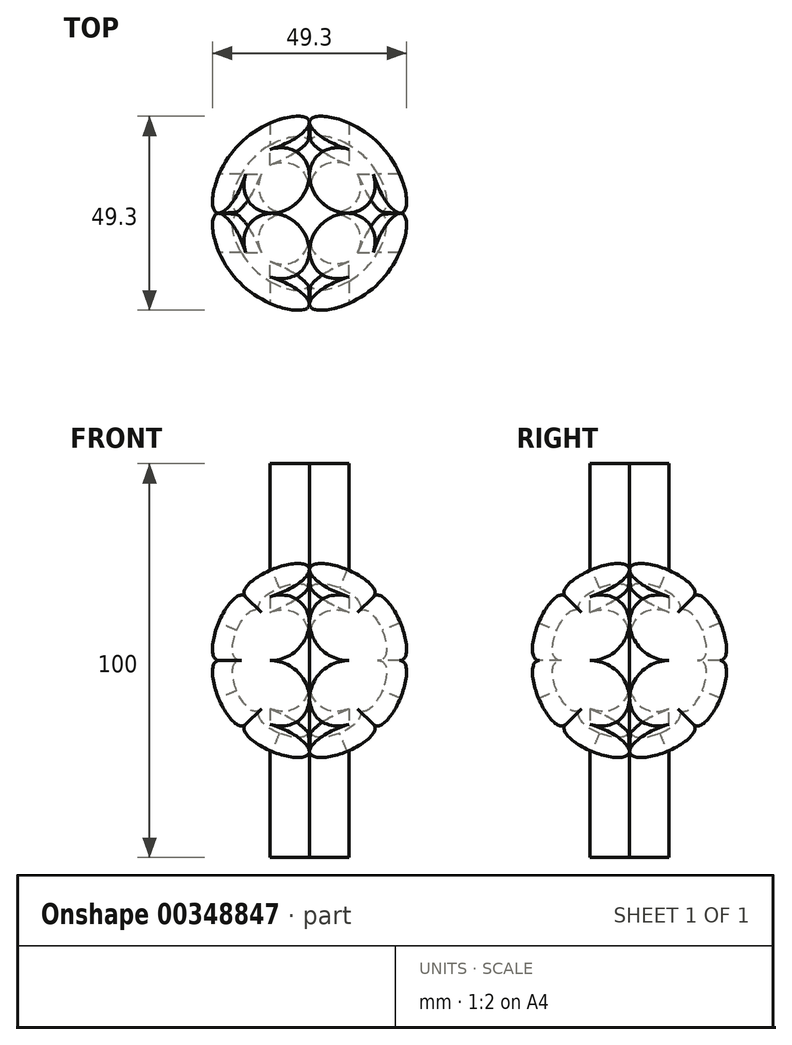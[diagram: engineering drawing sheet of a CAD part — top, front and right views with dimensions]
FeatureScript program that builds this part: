
annotation { "Feature Type Name" : "Feature", "Feature Type Description" : "" }
export const myFeature = defineFeature(function(context is Context, id is Id, definition is map)
    precondition{}
    {
        {
            var Q0;
            Q0=qCreatedBy(makeId("Front.planeOp"),FACE);
            var sketch = newSketch(context, id + "F0", { "sketchPlane" : qUnion([Q0])});
            skArc(sketch, "E0", {"start": v(0, -25) * mm, "mid": v(25, 0) * mm, "end": v(0, 25) * mm});
            skLineSegment(sketch, "E1", {"start": v(0, 25) * mm, "end": v(0, 20) * mm});
            skArc(sketch, "E2.0", {"start": v(0, -20) * mm, "mid": v(20, 0) * mm, "end": v(0, 20) * mm});
            skLineSegment(sketch, "E3.trimOffspring", {"start": v(0, -20) * mm, "end": v(0, -25) * mm});
            skSolve(sketch);
        }
        {
            var Q0;
            {var subQ0=sQuery(id+"F0.wireOp",EDGE,"E0");Q0=makeQuery(id+"F0.imprint","IMPRINT",FACE,{"disambiguationData":[TD([[makeQuery(id+"F0.imprint","IMPRINT",EDGE,{"derivedFrom":subQ0}),1.0]])]});}
            var Q1;
            Q1=sQuery(id+"F0.wireOp",EDGE,"E1");
            revolve(context, id + "F1", {"entities" : qUnion([Q0]), "axis" : qUnion([Q1]), "revolveType" : RevolveType.FULL});
        }
        {
            var Q0;
            Q0=qCreatedBy(makeId("Front.planeOp"),FACE);
            var sketch = newSketch(context, id + "F2", { "sketchPlane" : qUnion([Q0])});
            skArc(sketch, "E4", {"start": v(0, 10) * mm, "mid": v(2.93, 2.93) * mm, "end": v(10, 0) * mm});
            skArc(sketch, "E5.1.0", {"start": v(-10, 0) * mm, "mid": v(-2.93, 2.93) * mm, "end": v(0, 10) * mm});
            skArc(sketch, "E5.2.0", {"start": v(0, -10) * mm, "mid": v(-2.93, -2.93) * mm, "end": v(-10, 0) * mm});
            skArc(sketch, "E5.3.0", {"start": v(10, 0) * mm, "mid": v(2.93, -2.93) * mm, "end": v(0, -10) * mm});
            skPoint(sketch, "E5.center", {"position": v(0, 0) * mm});
            skSolve(sketch);
        }
        {
            var Q0;
            Q0=makeQuery(id+"F2.imprint","IMPRINT",FACE,{"disambiguationData":[TD([[makeQuery(id+"F2.imprint","IMPRINT",EDGE,{"derivedFrom":sQuery(id+"F2.wireOp",EDGE,"E4")}),-1.0]])]});
            extrude(context, id + "F3", {"entities" : qUnion([Q0]), "endBound" : BoundingType.SYMMETRIC, "oppositeDirection" : true, "depth" : 100 * mm, "hasSecondDirection" : true, "secondDirectionBound" : SecondDirectionBoundingType.THROUGH_ALL, "secondDirectionOppositeDirection" : false, "secondDirectionDepth" : 25 * mm});
        }
        {
            var Q0;
            Q0=qCreatedBy(makeId("Top.planeOp"),FACE);
            var sketch = newSketch(context, id + "F4", { "sketchPlane" : qUnion([Q0])});
            skLineSegment(sketch, "E6", {"start": v(-40.96, 0) * mm, "end": v(40.96, 0) * mm, "construction": true});
            skLineSegment(sketch, "E7", {"start": v(0, 49.6) * mm, "end": v(0, -63.23) * mm, "construction": true});
            skSolve(sketch);
        }
        {
            var Q0;
            Q0=makeQuery(id+"F3.opExtrude","SWEPT_BODY",BODY,{"disambiguationData":[OSD([sQuery(id+"F2.wireOp",EDGE,"E4"),sQuery(id+"F2.wireOp",EDGE,"E5.1.0"),sQuery(id+"F2.wireOp",EDGE,"E5.2.0"),sQuery(id+"F2.wireOp",EDGE,"E5.3.0")])]});
            var Q1;
            Q1=sQuery(id+"F4.wireOp",EDGE,"E6");
            circularPattern(context, id + "F5", {"entities" : qUnion([Q0]), "axis" : qUnion([Q1]), "angle" : 360 * degree, "instanceCount" : 8, "equalSpace" : true});
        }
        {
            var Q0;
            Q0=qCreatedBy(makeId("Right.planeOp"),FACE);
            var sketch = newSketch(context, id + "F6", { "sketchPlane" : qUnion([Q0])});
            skLineSegment(sketch, "E8", {"start": v(-65.3, 0) * mm, "end": v(60.96, 0) * mm, "construction": true});
            skLineSegment(sketch, "E9", {"start": v(0, 65.88) * mm, "end": v(0, -65.12) * mm, "construction": true});
            skSolve(sketch);
        }
        {
            var Q0;
            Q0=makeQuery(id+"F5.opPattern","COPY",BODY,{"derivedFrom":makeQuery(id+"F3.opExtrude","SWEPT_BODY",BODY,{"disambiguationData":[OSD([sQuery(id+"F2.wireOp",EDGE,"E4"),sQuery(id+"F2.wireOp",EDGE,"E5.1.0"),sQuery(id+"F2.wireOp",EDGE,"E5.2.0"),sQuery(id+"F2.wireOp",EDGE,"E5.3.0")])]}),"instanceName":"2"});
            var Q1;
            Q1=sQuery(id+"F6.wireOp",EDGE,"E8");
            circularPattern(context, id + "F7", {"entities" : qUnion([Q0]), "axis" : qUnion([Q1]), "angle" : 360 * degree, "instanceCount" : 8, "equalSpace" : true});
        }
        {
            var Q0;
            Q0=makeQuery(id+"F3.opExtrude","SWEPT_BODY",BODY,{"disambiguationData":[OSD([sQuery(id+"F2.wireOp",EDGE,"E4"),sQuery(id+"F2.wireOp",EDGE,"E5.1.0"),sQuery(id+"F2.wireOp",EDGE,"E5.2.0"),sQuery(id+"F2.wireOp",EDGE,"E5.3.0")])]});
            var Q1;
            Q1=makeQuery(id+"F5.opPattern","COPY",BODY,{"derivedFrom":makeQuery(id+"F3.opExtrude","SWEPT_BODY",BODY,{"disambiguationData":[OSD([sQuery(id+"F2.wireOp",EDGE,"E4"),sQuery(id+"F2.wireOp",EDGE,"E5.1.0"),sQuery(id+"F2.wireOp",EDGE,"E5.2.0"),sQuery(id+"F2.wireOp",EDGE,"E5.3.0")])]}),"instanceName":"1"});
            var Q2;
            Q2=makeQuery(id+"F5.opPattern","COPY",BODY,{"derivedFrom":makeQuery(id+"F3.opExtrude","SWEPT_BODY",BODY,{"disambiguationData":[OSD([sQuery(id+"F2.wireOp",EDGE,"E4"),sQuery(id+"F2.wireOp",EDGE,"E5.1.0"),sQuery(id+"F2.wireOp",EDGE,"E5.2.0"),sQuery(id+"F2.wireOp",EDGE,"E5.3.0")])]}),"instanceName":"3"});
            var Q3;
            Q3=makeQuery(id+"F5.opPattern","COPY",BODY,{"derivedFrom":makeQuery(id+"F3.opExtrude","SWEPT_BODY",BODY,{"disambiguationData":[OSD([sQuery(id+"F2.wireOp",EDGE,"E4"),sQuery(id+"F2.wireOp",EDGE,"E5.1.0"),sQuery(id+"F2.wireOp",EDGE,"E5.2.0"),sQuery(id+"F2.wireOp",EDGE,"E5.3.0")])]}),"instanceName":"5"});
            var Q4;
            Q4=makeQuery(id+"F5.opPattern","COPY",BODY,{"derivedFrom":makeQuery(id+"F3.opExtrude","SWEPT_BODY",BODY,{"disambiguationData":[OSD([sQuery(id+"F2.wireOp",EDGE,"E4"),sQuery(id+"F2.wireOp",EDGE,"E5.1.0"),sQuery(id+"F2.wireOp",EDGE,"E5.2.0"),sQuery(id+"F2.wireOp",EDGE,"E5.3.0")])]}),"instanceName":"7"});
            var Q5;
            Q5=makeQuery(id+"F7.opPattern","COPY",BODY,{"derivedFrom":makeQuery(id+"F5.opPattern","COPY",BODY,{"derivedFrom":makeQuery(id+"F3.opExtrude","SWEPT_BODY",BODY,{"disambiguationData":[OSD([sQuery(id+"F2.wireOp",EDGE,"E4"),sQuery(id+"F2.wireOp",EDGE,"E5.1.0"),sQuery(id+"F2.wireOp",EDGE,"E5.2.0"),sQuery(id+"F2.wireOp",EDGE,"E5.3.0")])]}),"instanceName":"2"}),"instanceName":"2"});
            var Q6;
            Q6=makeQuery(id+"F7.opPattern","COPY",BODY,{"derivedFrom":makeQuery(id+"F5.opPattern","COPY",BODY,{"derivedFrom":makeQuery(id+"F3.opExtrude","SWEPT_BODY",BODY,{"disambiguationData":[OSD([sQuery(id+"F2.wireOp",EDGE,"E4"),sQuery(id+"F2.wireOp",EDGE,"E5.1.0"),sQuery(id+"F2.wireOp",EDGE,"E5.2.0"),sQuery(id+"F2.wireOp",EDGE,"E5.3.0")])]}),"instanceName":"2"}),"instanceName":"5"});
            var Q7;
            Q7=makeQuery(id+"F7.opPattern","COPY",BODY,{"derivedFrom":makeQuery(id+"F5.opPattern","COPY",BODY,{"derivedFrom":makeQuery(id+"F3.opExtrude","SWEPT_BODY",BODY,{"disambiguationData":[OSD([sQuery(id+"F2.wireOp",EDGE,"E4"),sQuery(id+"F2.wireOp",EDGE,"E5.1.0"),sQuery(id+"F2.wireOp",EDGE,"E5.2.0"),sQuery(id+"F2.wireOp",EDGE,"E5.3.0")])]}),"instanceName":"2"}),"instanceName":"6"});
            var Q8;
            Q8=makeQuery(id+"F7.opPattern","COPY",BODY,{"derivedFrom":makeQuery(id+"F5.opPattern","COPY",BODY,{"derivedFrom":makeQuery(id+"F3.opExtrude","SWEPT_BODY",BODY,{"disambiguationData":[OSD([sQuery(id+"F2.wireOp",EDGE,"E4"),sQuery(id+"F2.wireOp",EDGE,"E5.1.0"),sQuery(id+"F2.wireOp",EDGE,"E5.2.0"),sQuery(id+"F2.wireOp",EDGE,"E5.3.0")])]}),"instanceName":"2"}),"instanceName":"7"});
            var Q9;
            Q9=makeQuery(id+"F7.opPattern","COPY",BODY,{"derivedFrom":makeQuery(id+"F5.opPattern","COPY",BODY,{"derivedFrom":makeQuery(id+"F3.opExtrude","SWEPT_BODY",BODY,{"disambiguationData":[OSD([sQuery(id+"F2.wireOp",EDGE,"E4"),sQuery(id+"F2.wireOp",EDGE,"E5.1.0"),sQuery(id+"F2.wireOp",EDGE,"E5.2.0"),sQuery(id+"F2.wireOp",EDGE,"E5.3.0")])]}),"instanceName":"2"}),"instanceName":"4"});
            var Q10;
            Q10=makeQuery(id+"F7.opPattern","COPY",BODY,{"derivedFrom":makeQuery(id+"F5.opPattern","COPY",BODY,{"derivedFrom":makeQuery(id+"F3.opExtrude","SWEPT_BODY",BODY,{"disambiguationData":[OSD([sQuery(id+"F2.wireOp",EDGE,"E4"),sQuery(id+"F2.wireOp",EDGE,"E5.1.0"),sQuery(id+"F2.wireOp",EDGE,"E5.2.0"),sQuery(id+"F2.wireOp",EDGE,"E5.3.0")])]}),"instanceName":"2"}),"instanceName":"3"});
            var Q11;
            Q11=makeQuery(id+"F7.opPattern","COPY",BODY,{"derivedFrom":makeQuery(id+"F5.opPattern","COPY",BODY,{"derivedFrom":makeQuery(id+"F3.opExtrude","SWEPT_BODY",BODY,{"disambiguationData":[OSD([sQuery(id+"F2.wireOp",EDGE,"E4"),sQuery(id+"F2.wireOp",EDGE,"E5.1.0"),sQuery(id+"F2.wireOp",EDGE,"E5.2.0"),sQuery(id+"F2.wireOp",EDGE,"E5.3.0")])]}),"instanceName":"2"}),"instanceName":"1"});
            var Q12;
            Q12=makeQuery(id+"F5.opPattern","COPY",BODY,{"derivedFrom":makeQuery(id+"F3.opExtrude","SWEPT_BODY",BODY,{"disambiguationData":[OSD([sQuery(id+"F2.wireOp",EDGE,"E4"),sQuery(id+"F2.wireOp",EDGE,"E5.1.0"),sQuery(id+"F2.wireOp",EDGE,"E5.2.0"),sQuery(id+"F2.wireOp",EDGE,"E5.3.0")])]}),"instanceName":"6"});
            var Q13;
            Q13=makeQuery(id+"F5.opPattern","COPY",BODY,{"derivedFrom":makeQuery(id+"F3.opExtrude","SWEPT_BODY",BODY,{"disambiguationData":[OSD([sQuery(id+"F2.wireOp",EDGE,"E4"),sQuery(id+"F2.wireOp",EDGE,"E5.1.0"),sQuery(id+"F2.wireOp",EDGE,"E5.2.0"),sQuery(id+"F2.wireOp",EDGE,"E5.3.0")])]}),"instanceName":"6"});
            var Q14;
            Q14=makeQuery(id+"F5.opPattern","COPY",BODY,{"derivedFrom":makeQuery(id+"F3.opExtrude","SWEPT_BODY",BODY,{"disambiguationData":[OSD([sQuery(id+"F2.wireOp",EDGE,"E4"),sQuery(id+"F2.wireOp",EDGE,"E5.1.0"),sQuery(id+"F2.wireOp",EDGE,"E5.2.0"),sQuery(id+"F2.wireOp",EDGE,"E5.3.0")])]}),"instanceName":"4"});
            var Q15;
            Q15=makeQuery(id+"F1.opRevolve","SWEPT_BODY",BODY,{"disambiguationData":[OSD([sQuery(id+"F0.wireOp",EDGE,"E0"),sQuery(id+"F0.wireOp",EDGE,"E1"),sQuery(id+"F0.wireOp",EDGE,"E2.0"),sQuery(id+"F0.wireOp",EDGE,"E3.trimOffspring")])]});
            booleanBodies(context, id + "F8", {"operationType" : BooleanOperationType.SUBTRACTION, "tools" : qUnion([Q0, Q1, Q2, Q3, Q4, Q5, Q6, Q7, Q8, Q9, Q10, Q11, Q12, Q13, Q14]), "targets" : qUnion([Q15])});
        }
    });
